# Revit family: JC KONTAKTER JCK250 FI
name_source: partatom
category: Specialty Equipment
units: mm (PartAtom-declared; Revit-internal decimal feet)

## family parameters
Cut with Voids When Loaded = No
Enable Cutting in Views = Yes
Host = Face
Maintain Annotation Orientation = Yes
Part Type = Normal
Room Calculation Point = No
Round Connector Dimension = Use Diameter
Shared = No

## types (1)
- JCK250
    CE asiakirja = https://jckontakter.se
    Default Elevation = 800 mm  [stored 2.62467 ft]
    Description = JCK250 on vain 50 mm leveä ja se on suunniteltu asennettavaksi lasipintoihin, joissa on 50 mm profiilijärjestelmä, sekä muihin tiloihin, joissa tilaa on rajoitetusti. Malli on valmistettu hopeanväriseksi anodisoidusta alumiinista mustilla päätykappaleilla, ja siinä on kaksi kosketustuntuisen uran, jotka tarjoavat lisäohjausta näkörajoitteisille henkilöille. Näin voidaan helposti tunnustella, mistä kohtaa tulee painaa oven avaamisen aktivoimiseksi.
    Kansi = Aluminum ENAW 6060
    Kotelo = Aluminum ENAW 6060
    Manufacturer = JC Kontakter
    Mikrokytkimien määrä = 1
    Mikrokytkin = Standar NO IP67
    Model = JCK250
    Nimellisestä nimellisvirrasta = 1mA/4 V DC
    Pienin nimellisvirta = 12V Resistiivinen 6A Induktiivinen L/R 5ms 6A, 24V Resistiivinen 6A Induktiivinen L/R 5ms 5A
    Päätypäät = POM Tenac C 4520
    Tekniken tuotekortti = https://www.jckontakter.fi
    Tuotteen paino = 0.263 kg
    URL = https://www.jckontakter.fi
    Valmistusmaa = Ruotsi

note: [stored X ft] marks values corroborated as IEEE doubles in the binary element streams (Revit-internal decimal feet)

## geometry (parser evidence)
native form markers: Sweep x5
no freeform markers — native parametric forms only
